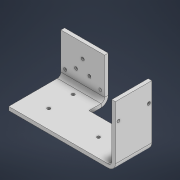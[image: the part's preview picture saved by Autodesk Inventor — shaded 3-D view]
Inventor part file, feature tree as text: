
AUTODESK INVENTOR PART (.ipt)
format: ipt  version: 2021 (Build 250183000, 183)  size: 214,016 bytes
history: native  units: mm
features: sheet_metal_op x9, sketch x7, other x4, hole x3, mirror x1, plane x1, split x1
ambient origin geometry x8: Origin, YZ Plane, XZ Plane, XY Plane, X Axis, Y Axis, Z Axis, Center Point
bodies: Solid1 (feature_tree)
feature tree (26):
  sheet_metal_op  "Face1"
  sheet_metal_op  "Flange1"
  sheet_metal_op  "Face2"
  sheet_metal_op  "Flange2"
  hole  "Hole1"  [1 undecoded]
  hole  "Hole2"  [1 undecoded]
  hole  "Hole3"  [1 undecoded]
  mirror  "Mirror1"
  plane  "Work Plane1"
  split  "Split1"
  sketch  "Sketch1"  dims[d0=72.0mm d1=36.0mm]
  other  "Plate1"
  sketch  "Sketch2"  dims[d2=72.0mm d3=36.0mm]
  other  "Plate2"
  sheet_metal_op  "Bend1"
  sheet_metal_op  "Corner1"
  sketch  "Sketch3"  dims[d4=6.0mm d5=6.0mm]
  other  "Plate3"
  sheet_metal_op  "Bend2"
  sketch  "Sketch4"  dims[d6=3.0mm]
  other  "Plate4"
  sheet_metal_op  "Bend3"
  sheet_metal_op  "Corner2"
  sketch  "Sketch5"  dims[d7=12.0mm]
  sketch  "Sketch6"  dims[d8=6.0mm]
  sketch  "Sketch7"  dims[d9=92.0mm d10=90.0deg d11=6.0mm d12=24.0mm d13=6.0mm d14=6.0mm d15=103.7mm d16=60.0mm d17=6.0mm d18=6.0mm d19=3.0mm d20=12.0mm d21=6.0mm d22=6.0mm d23=3.0mm d24=12.0mm d25=6.0mm d26=100.6mm d27=90.0deg d28=6.0mm d29=24.0mm d30=6.0mm d31=6.0mm d32=60.0mm d33=30.0mm d34=30.0mm d35=50.0mm d36=30.0mm d37=30.0mm d38=5.0mm d39=6.0mm d40=4.0mm d41=2.0mm d42=90.0deg d43=6.0mm d44=0.0mm d45=36.0mm d46=25.4mm d47=67.0mm d48=120.0deg d49=120.0deg d50=0.0mm d51=5.0mm d52=6.0mm d53=4.0mm d54=2.0mm d55=90.0deg d56=6.0mm d57=0.0mm d58=5.0mm d59=6.0mm d60=4.0mm d61=2.0mm d62=90.0deg d63=6.0mm d64=0.0mm d65=60.0mm d66=72.0mm d67=30.0mm d68=30.0mm d69=36.0mm d70=20.0mm d71=10.0mm d72=36.0mm d73=91.7mm d74=45.85mm]
note: 3 required parameter values undecoded (feature->parameter linkage not recoverable at this tier; creation-order binding heuristic only, values carry confidence <= 0.55)
